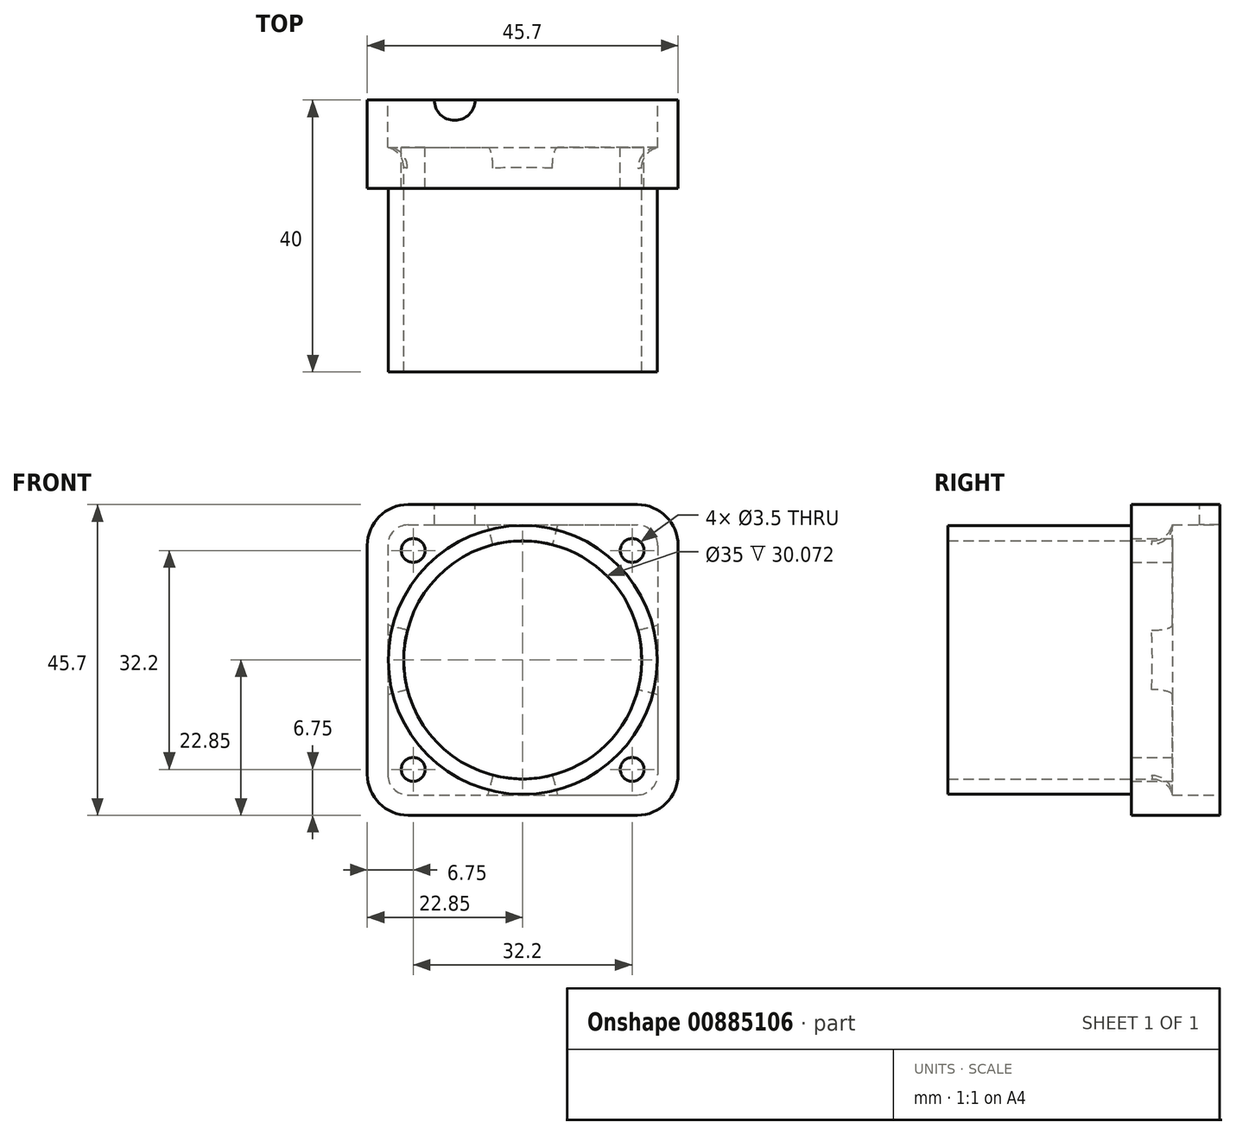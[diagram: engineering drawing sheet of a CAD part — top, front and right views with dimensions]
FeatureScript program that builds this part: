
annotation { "Feature Type Name" : "Feature", "Feature Type Description" : "" }
export const myFeature = defineFeature(function(context is Context, id is Id, definition is map)
    precondition{}
    {
        {
            var Q0;
            Q0=qCreatedBy(makeId("Front.planeOp"),FACE);
            var sketch = newSketch(context, id + "F0", { "sketchPlane" : qUnion([Q0])});
            skLineSegment(sketch, "E0.bottom", {"start": v(-16.85, 19.85) * mm, "end": v(16.85, 19.85) * mm});
            skLineSegment(sketch, "E0.top", {"start": v(-16.85, -19.85) * mm, "end": v(16.85, -19.85) * mm});
            skLineSegment(sketch, "E0.left", {"start": v(-19.85, 16.85) * mm, "end": v(-19.85, -16.85) * mm});
            skLineSegment(sketch, "E0.right", {"start": v(19.85, 16.85) * mm, "end": v(19.85, -16.85) * mm});
            skPoint(sketch, "E1.visualSharp", {"position": v(-19.85, 19.85) * mm});
            skArc(sketch, "E1.filletArc", {"start": v(-16.85, 19.85) * mm, "mid": v(-18.97, 18.97) * mm, "end": v(-19.85, 16.85) * mm});
            skPoint(sketch, "E2.visualSharp", {"position": v(19.85, 19.85) * mm});
            skArc(sketch, "E2.filletArc", {"start": v(19.85, 16.85) * mm, "mid": v(18.97, 18.97) * mm, "end": v(16.85, 19.85) * mm});
            skPoint(sketch, "E3.visualSharp", {"position": v(19.85, -19.85) * mm});
            skArc(sketch, "E3.filletArc", {"start": v(16.85, -19.85) * mm, "mid": v(18.97, -18.97) * mm, "end": v(19.85, -16.85) * mm});
            skPoint(sketch, "E4.visualSharp", {"position": v(-19.85, -19.85) * mm});
            skArc(sketch, "E4.filletArc", {"start": v(-19.85, -16.85) * mm, "mid": v(-18.97, -18.97) * mm, "end": v(-16.85, -19.85) * mm});
            skLineSegment(sketch, "E5", {"start": v(0, 39.42) * mm, "end": v(0, -47.6) * mm, "construction": true});
            skLineSegment(sketch, "E6", {"start": v(-47.09, 0) * mm, "end": v(48.42, 0) * mm, "construction": true});
            skArc(sketch, "E7.0", {"start": v(-16.85, 22.85) * mm, "mid": v(-21.1, 21.1) * mm, "end": v(-22.85, 16.85) * mm});
            skLineSegment(sketch, "E7.1", {"start": v(-16.85, 22.85) * mm, "end": v(16.85, 22.85) * mm});
            skLineSegment(sketch, "E7.2", {"start": v(-22.85, 16.85) * mm, "end": v(-22.85, -16.85) * mm});
            skArc(sketch, "E7.3", {"start": v(22.85, 16.85) * mm, "mid": v(21.1, 21.1) * mm, "end": v(16.85, 22.85) * mm});
            skArc(sketch, "E7.4", {"start": v(-22.85, -16.85) * mm, "mid": v(-21.1, -21.1) * mm, "end": v(-16.85, -22.85) * mm});
            skLineSegment(sketch, "E7.5", {"start": v(-16.85, -22.85) * mm, "end": v(16.85, -22.85) * mm});
            skArc(sketch, "E7.6", {"start": v(16.85, -22.85) * mm, "mid": v(21.1, -21.1) * mm, "end": v(22.85, -16.85) * mm});
            skLineSegment(sketch, "E7.7", {"start": v(22.85, 16.85) * mm, "end": v(22.85, -16.85) * mm});
            skSolve(sketch);
        }
        {
            var Q0;
            Q0 = qSketchRegion(id + "F0", true);
            extrude(context, id + "F1", {"entities" : qUnion([Q0]), "depth" : 40 * mm, "offsetDistance" : 25 * mm});
        }
        {
            var Q0;
            Q0=makeQuery(id+"F1.opExtrude","CAP_FACE",FACE,{"disambiguationData":[OSD([sQuery(id+"F0.wireOp",EDGE,"E0.bottom"),sQuery(id+"F0.wireOp",EDGE,"E0.top"),sQuery(id+"F0.wireOp",EDGE,"E0.left"),sQuery(id+"F0.wireOp",EDGE,"E0.right"),sQuery(id+"F0.wireOp",EDGE,"E1.filletArc"),sQuery(id+"F0.wireOp",EDGE,"E2.filletArc"),sQuery(id+"F0.wireOp",EDGE,"E3.filletArc"),sQuery(id+"F0.wireOp",EDGE,"E4.filletArc"),sQuery(id+"F0.wireOp",EDGE,"E7.0"),sQuery(id+"F0.wireOp",EDGE,"E7.1"),sQuery(id+"F0.wireOp",EDGE,"E7.2"),sQuery(id+"F0.wireOp",EDGE,"E7.3"),sQuery(id+"F0.wireOp",EDGE,"E7.4"),sQuery(id+"F0.wireOp",EDGE,"E7.5"),sQuery(id+"F0.wireOp",EDGE,"E7.6"),sQuery(id+"F0.wireOp",EDGE,"E7.7")])],"isStart":true});
            var sketch = newSketch(context, id + "F2", { "sketchPlane" : qUnion([Q0])});
            skCircle(sketch, "E8", {"center": v(0, 0) * mm, "radius": 17.5 * mm});
            skLineSegment(sketch, "E9.0", {"start": v(-19.85, 16.85) * mm, "end": v(-19.85, -16.85) * mm});
            skArc(sketch, "E9.1", {"start": v(-19.85, 16.85) * mm, "mid": v(-18.97, 18.97) * mm, "end": v(-16.85, 19.85) * mm});
            skLineSegment(sketch, "E9.2", {"start": v(16.85, 19.85) * mm, "end": v(-16.85, 19.85) * mm});
            skArc(sketch, "E9.3", {"start": v(16.85, 19.85) * mm, "mid": v(18.97, 18.97) * mm, "end": v(19.85, 16.85) * mm});
            skLineSegment(sketch, "E9.4", {"start": v(19.85, 16.85) * mm, "end": v(19.85, -16.85) * mm});
            skArc(sketch, "E9.5", {"start": v(19.85, -16.85) * mm, "mid": v(18.97, -18.97) * mm, "end": v(16.85, -19.85) * mm});
            skLineSegment(sketch, "E9.6", {"start": v(16.85, -19.85) * mm, "end": v(-16.85, -19.85) * mm});
            skArc(sketch, "E9.7", {"start": v(-16.85, -19.85) * mm, "mid": v(-18.97, -18.97) * mm, "end": v(-19.85, -16.85) * mm});
            skLineSegment(sketch, "E10.bottom", {"start": v(-16.1, 16.1) * mm, "end": v(16.1, 16.1) * mm, "construction": true});
            skLineSegment(sketch, "E10.top", {"start": v(-16.1, -16.1) * mm, "end": v(16.1, -16.1) * mm, "construction": true});
            skLineSegment(sketch, "E10.left", {"start": v(-16.1, 16.1) * mm, "end": v(-16.1, -16.1) * mm, "construction": true});
            skLineSegment(sketch, "E10.right", {"start": v(16.1, 16.1) * mm, "end": v(16.1, -16.1) * mm, "construction": true});
            skCircle(sketch, "E11", {"center": v(-16.1, 16.1) * mm, "radius": 1.75 * mm});
            skCircle(sketch, "E12", {"center": v(16.1, 16.1) * mm, "radius": 1.75 * mm});
            skCircle(sketch, "E13", {"center": v(16.1, -16.1) * mm, "radius": 1.75 * mm});
            skCircle(sketch, "E14", {"center": v(-16.1, -16.1) * mm, "radius": 1.75 * mm});
            skSolve(sketch);
        }
        {
            var Q0;
            Q0 = qSketchRegion(id + "F2", true);
            var Q1;
            Q1=makeQuery(id+"F1.opExtrude","CAP_FACE",FACE,{"disambiguationData":[OSD([sQuery(id+"F0.wireOp",EDGE,"E0.bottom"),sQuery(id+"F0.wireOp",EDGE,"E0.top"),sQuery(id+"F0.wireOp",EDGE,"E0.left"),sQuery(id+"F0.wireOp",EDGE,"E0.right"),sQuery(id+"F0.wireOp",EDGE,"E1.filletArc"),sQuery(id+"F0.wireOp",EDGE,"E2.filletArc"),sQuery(id+"F0.wireOp",EDGE,"E3.filletArc"),sQuery(id+"F0.wireOp",EDGE,"E4.filletArc"),sQuery(id+"F0.wireOp",EDGE,"E7.0"),sQuery(id+"F0.wireOp",EDGE,"E7.1"),sQuery(id+"F0.wireOp",EDGE,"E7.2"),sQuery(id+"F0.wireOp",EDGE,"E7.3"),sQuery(id+"F0.wireOp",EDGE,"E7.4"),sQuery(id+"F0.wireOp",EDGE,"E7.5"),sQuery(id+"F0.wireOp",EDGE,"E7.6"),sQuery(id+"F0.wireOp",EDGE,"E7.7")])],"isStart":false});
            extrude(context, id + "F3", {"entities" : qUnion([Q0]), "operationType" : NewBodyOperationType.ADD, "endBound" : BoundingType.UP_TO_SURFACE, "oppositeDirection" : true, "depth" : 10 * mm, "endBoundEntityFace" : qUnion([Q1]), "offsetDistance" : 25 * mm});
        }
        {
            var Q0;
            Q0=makeQuery(id+"F3.boolean.opBoolean","MERGE",FACE,{"derivedFrom":[makeQuery(id+"F1.opExtrude","CAP_FACE",FACE,{"disambiguationData":[OSD([sQuery(id+"F0.wireOp",EDGE,"E0.bottom"),sQuery(id+"F0.wireOp",EDGE,"E0.top"),sQuery(id+"F0.wireOp",EDGE,"E0.left"),sQuery(id+"F0.wireOp",EDGE,"E0.right"),sQuery(id+"F0.wireOp",EDGE,"E1.filletArc"),sQuery(id+"F0.wireOp",EDGE,"E2.filletArc"),sQuery(id+"F0.wireOp",EDGE,"E3.filletArc"),sQuery(id+"F0.wireOp",EDGE,"E4.filletArc"),sQuery(id+"F0.wireOp",EDGE,"E7.0"),sQuery(id+"F0.wireOp",EDGE,"E7.1"),sQuery(id+"F0.wireOp",EDGE,"E7.2"),sQuery(id+"F0.wireOp",EDGE,"E7.3"),sQuery(id+"F0.wireOp",EDGE,"E7.4"),sQuery(id+"F0.wireOp",EDGE,"E7.5"),sQuery(id+"F0.wireOp",EDGE,"E7.6"),sQuery(id+"F0.wireOp",EDGE,"E7.7")])],"isStart":true}),makeQuery(id+"F3.opExtrude","CAP_FACE",FACE,{"disambiguationData":[OSD([sQuery(id+"F2.wireOp",EDGE,"E8"),sQuery(id+"F2.wireOp",EDGE,"E9.0"),sQuery(id+"F2.wireOp",EDGE,"E9.1"),sQuery(id+"F2.wireOp",EDGE,"E9.2"),sQuery(id+"F2.wireOp",EDGE,"E9.3"),sQuery(id+"F2.wireOp",EDGE,"E9.4"),sQuery(id+"F2.wireOp",EDGE,"E9.5"),sQuery(id+"F2.wireOp",EDGE,"E9.6"),sQuery(id+"F2.wireOp",EDGE,"E9.7"),sQuery(id+"F2.wireOp",EDGE,"E11"),sQuery(id+"F2.wireOp",EDGE,"E12"),sQuery(id+"F2.wireOp",EDGE,"E13"),sQuery(id+"F2.wireOp",EDGE,"E14")])],"isStart":true})]});
            var sketch = newSketch(context, id + "F4", { "sketchPlane" : qUnion([Q0])});
            skLineSegment(sketch, "E15.0", {"start": v(19.85, 16.85) * mm, "end": v(19.85, -16.85) * mm});
            skArc(sketch, "E15.1", {"start": v(16.85, 19.85) * mm, "mid": v(18.97, 18.97) * mm, "end": v(19.85, 16.85) * mm});
            skLineSegment(sketch, "E15.2", {"start": v(16.85, 19.85) * mm, "end": v(-16.85, 19.85) * mm});
            skPoint(sketch, "E15.3", {"position": v(-19.85, 16.85) * mm});
            skLineSegment(sketch, "E15.4", {"start": v(-19.85, 16.85) * mm, "end": v(-19.85, -16.85) * mm});
            skArc(sketch, "E15.5", {"start": v(-19.85, 16.85) * mm, "mid": v(-18.97, 18.97) * mm, "end": v(-16.85, 19.85) * mm});
            skArc(sketch, "E15.6", {"start": v(-16.85, -19.85) * mm, "mid": v(-18.97, -18.97) * mm, "end": v(-19.85, -16.85) * mm});
            skLineSegment(sketch, "E15.7", {"start": v(16.85, -19.85) * mm, "end": v(-16.85, -19.85) * mm});
            skArc(sketch, "E15.8", {"start": v(19.85, -16.85) * mm, "mid": v(18.97, -18.97) * mm, "end": v(16.85, -19.85) * mm});
            skSolve(sketch);
        }
        {
            var Q0;
            Q0 = qSketchRegion(id + "F4", true);
            extrude(context, id + "F5", {"entities" : qUnion([Q0]), "operationType" : NewBodyOperationType.REMOVE, "oppositeDirection" : true, "depth" : 7 * mm, "offsetDistance" : 25 * mm});
        }
        {
            var Q0;
            Q0=makeQuery(id+"F3.boolean.opBoolean","MERGE",FACE,{"derivedFrom":[makeQuery(id+"F1.opExtrude","CAP_FACE",FACE,{"disambiguationData":[OSD([sQuery(id+"F0.wireOp",EDGE,"E0.bottom"),sQuery(id+"F0.wireOp",EDGE,"E0.top"),sQuery(id+"F0.wireOp",EDGE,"E0.left"),sQuery(id+"F0.wireOp",EDGE,"E0.right"),sQuery(id+"F0.wireOp",EDGE,"E1.filletArc"),sQuery(id+"F0.wireOp",EDGE,"E2.filletArc"),sQuery(id+"F0.wireOp",EDGE,"E3.filletArc"),sQuery(id+"F0.wireOp",EDGE,"E4.filletArc"),sQuery(id+"F0.wireOp",EDGE,"E7.0"),sQuery(id+"F0.wireOp",EDGE,"E7.1"),sQuery(id+"F0.wireOp",EDGE,"E7.2"),sQuery(id+"F0.wireOp",EDGE,"E7.3"),sQuery(id+"F0.wireOp",EDGE,"E7.4"),sQuery(id+"F0.wireOp",EDGE,"E7.5"),sQuery(id+"F0.wireOp",EDGE,"E7.6"),sQuery(id+"F0.wireOp",EDGE,"E7.7")])],"isStart":false}),makeQuery(id+"F3.opExtrude","CAP_FACE",FACE,{"disambiguationData":[OSD([sQuery(id+"F2.wireOp",EDGE,"E8"),sQuery(id+"F2.wireOp",EDGE,"E9.0"),sQuery(id+"F2.wireOp",EDGE,"E9.1"),sQuery(id+"F2.wireOp",EDGE,"E9.2"),sQuery(id+"F2.wireOp",EDGE,"E9.3"),sQuery(id+"F2.wireOp",EDGE,"E9.4"),sQuery(id+"F2.wireOp",EDGE,"E9.5"),sQuery(id+"F2.wireOp",EDGE,"E9.6"),sQuery(id+"F2.wireOp",EDGE,"E9.7"),sQuery(id+"F2.wireOp",EDGE,"E11"),sQuery(id+"F2.wireOp",EDGE,"E12"),sQuery(id+"F2.wireOp",EDGE,"E13"),sQuery(id+"F2.wireOp",EDGE,"E14")])],"isStart":false})]});
            var sketch = newSketch(context, id + "F6", { "sketchPlane" : qUnion([Q0])});
            skCircle(sketch, "E16", {"center": v(0, 0) * mm, "radius": 19.77 * mm});
            skCircle(sketch, "E17", {"center": v(-16.1, 16.1) * mm, "radius": 3 * mm, "construction": true});
            skCircle(sketch, "E18", {"center": v(0, 0) * mm, "radius": 29.83 * mm});
            skSolve(sketch);
        }
        {
            var Q0;
            Q0 = qSketchRegion(id + "F6", true);
            extrude(context, id + "F7", {"entities" : qUnion([Q0]), "operationType" : NewBodyOperationType.REMOVE, "oppositeDirection" : true, "depth" : 27 * mm, "offsetDistance" : 25 * mm});
        }
        {
            var Q0;
            Q0=makeQuery(id+"F5.boolean.opBoolean","INTERSECT",EDGE,{"derivedFrom":[makeQuery(id+"F3.opExtrude","SWEPT_FACE",FACE,{"disambiguationData":[OSD([sQuery(id+"F2.wireOp",EDGE,"E8")])]}),makeQuery(id+"F5.opExtrude","CAP_FACE",FACE,{"disambiguationData":[OSD([sQuery(id+"F4.wireOp",EDGE,"E15.0"),sQuery(id+"F4.wireOp",EDGE,"E15.1"),sQuery(id+"F4.wireOp",EDGE,"E15.2"),sQuery(id+"F4.wireOp",EDGE,"E15.4"),sQuery(id+"F4.wireOp",EDGE,"E15.5"),sQuery(id+"F4.wireOp",EDGE,"E15.6"),sQuery(id+"F4.wireOp",EDGE,"E15.7"),sQuery(id+"F4.wireOp",EDGE,"E15.8")])],"isStart":false})]});
            fillet(context, id + "F8", {"entities" : qUnion([Q0]), "radius" : 3 * mm, "tangentPropagation" : true, "allowEdgeOverflow" : false});
        }
        {
            var Q0;
            Q0=makeQuery(id+"F1.opExtrude","SWEPT_FACE",FACE,{"disambiguationData":[OSD([sQuery(id+"F0.wireOp",EDGE,"E7.1")])]});
            var sketch = newSketch(context, id + "F9", { "sketchPlane" : qUnion([Q0])});
            skCircle(sketch, "E19", {"center": v(-10, 0) * mm, "radius": 3 * mm});
            skSolve(sketch);
        }
        {
            var Q0;
            Q0 = qSketchRegion(id + "F9", true);
            extrude(context, id + "F10", {"entities" : qUnion([Q0]), "operationType" : NewBodyOperationType.REMOVE, "endBound" : BoundingType.UP_TO_NEXT, "oppositeDirection" : true, "depth" : 25 * mm, "offsetDistance" : 25 * mm});
        }
    });
